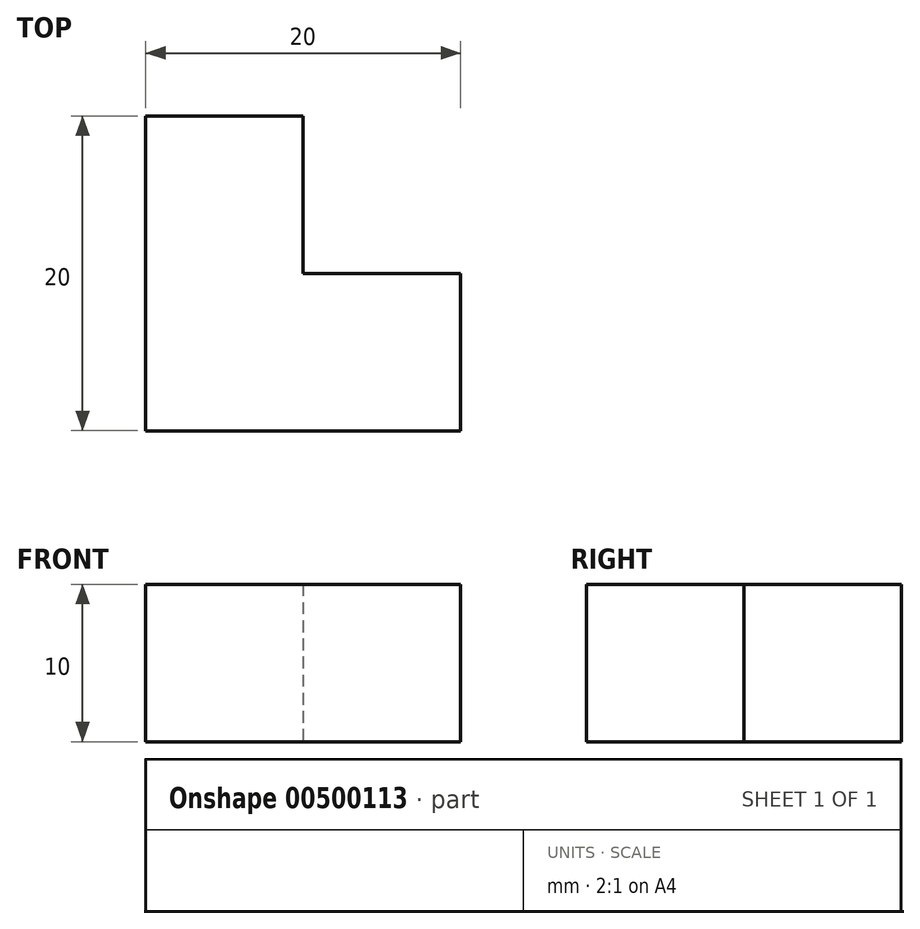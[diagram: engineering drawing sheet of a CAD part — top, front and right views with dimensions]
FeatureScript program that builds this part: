
annotation { "Feature Type Name" : "Feature", "Feature Type Description" : "" }
export const myFeature = defineFeature(function(context is Context, id is Id, definition is map)
    precondition{}
    {
        {
            var Q0;
            Q0=qCreatedBy(makeId("Top.planeOp"),FACE);
            var sketch = newSketch(context, id + "F0", { "sketchPlane" : qUnion([Q0])});
            skLineSegment(sketch, "E0", {"start": v(-44.77, 3.59) * mm, "end": v(-44.77, -16.41) * mm});
            skLineSegment(sketch, "E1", {"start": v(-44.77, -16.41) * mm, "end": v(-24.77, -16.41) * mm});
            skLineSegment(sketch, "E2", {"start": v(-24.77, -16.41) * mm, "end": v(-24.77, -6.41) * mm});
            skLineSegment(sketch, "E3", {"start": v(-24.77, -6.41) * mm, "end": v(-34.77, -6.41) * mm});
            skLineSegment(sketch, "E4", {"start": v(-34.77, -6.41) * mm, "end": v(-34.77, 3.59) * mm});
            skLineSegment(sketch, "E5", {"start": v(-34.77, 3.59) * mm, "end": v(-44.77, 3.59) * mm});
            skSolve(sketch);
        }
        {
            var Q0;
            Q0=makeQuery(id+"F0.imprint","IMPRINT",FACE,{"disambiguationData":[TD([[makeQuery(id+"F0.imprint","IMPRINT",EDGE,{"derivedFrom":sQuery(id+"F0.wireOp",EDGE,"E0")}),1.0]])]});
            extrude(context, id + "F1", {"entities" : qUnion([Q0]), "depth" : 10 * mm});
        }
    });
